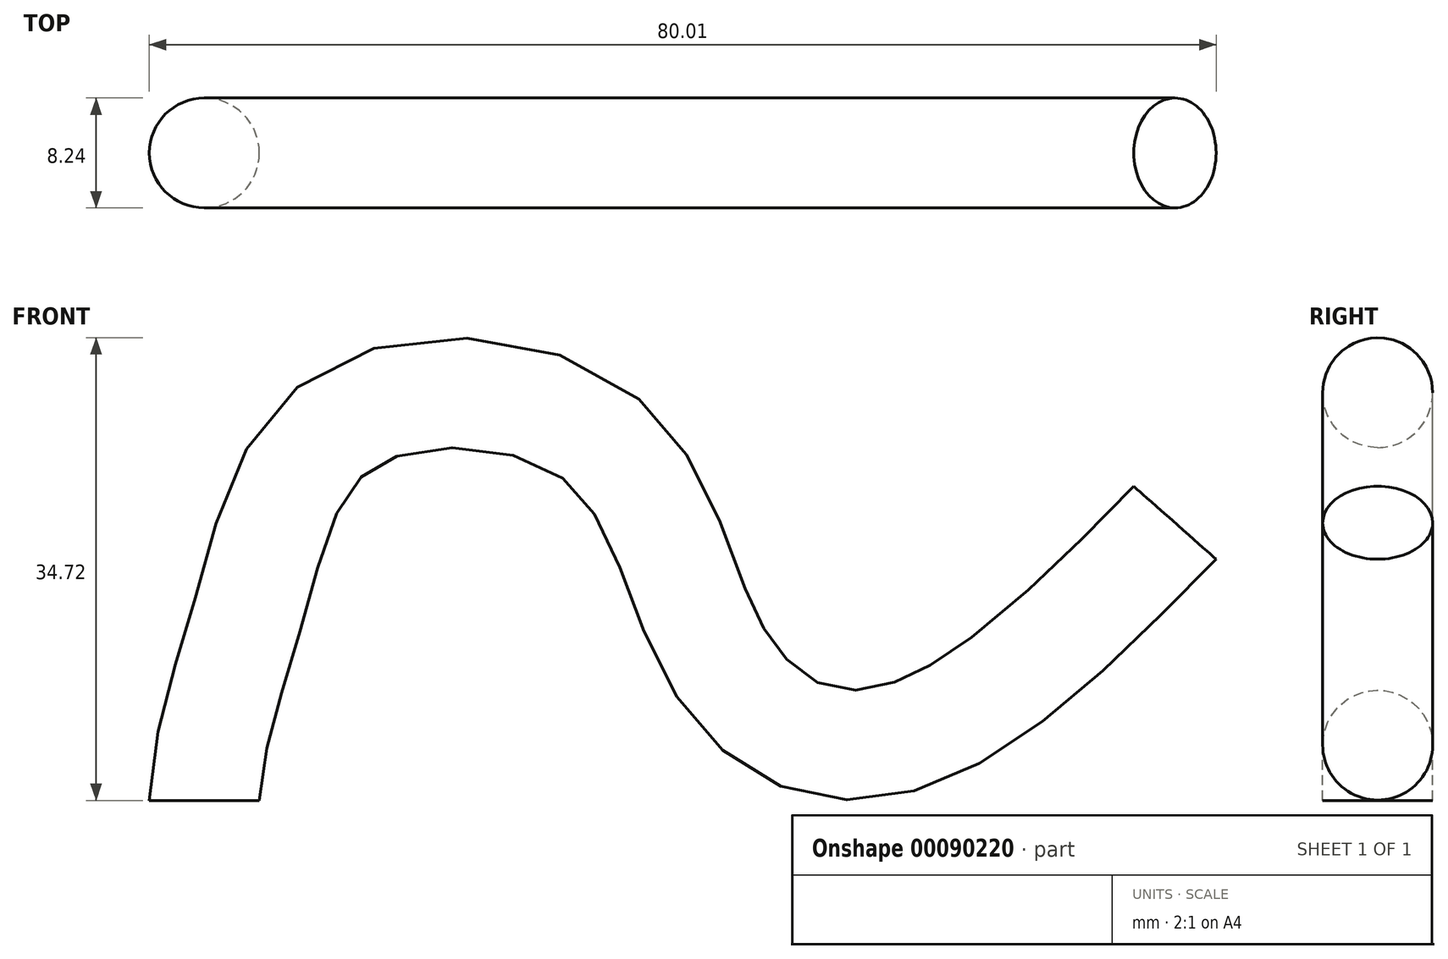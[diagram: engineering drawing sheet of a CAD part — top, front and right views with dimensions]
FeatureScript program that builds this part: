
annotation { "Feature Type Name" : "Feature", "Feature Type Description" : "" }
export const myFeature = defineFeature(function(context is Context, id is Id, definition is map)
    precondition{}
    {
        {
            var Q0;
            Q0=qCreatedBy(makeId("Front.planeOp"),FACE);
            var sketch = newSketch(context, id + "F0", { "sketchPlane" : qUnion([Q0])});
            skPoint(sketch, "E0", {"position": v(-50.34, 0) * mm});
            skPoint(sketch, "E1", {"position": v(-46.87, 14.66) * mm});
            skPoint(sketch, "E2", {"position": v(-39.95, 28.29) * mm});
            skPoint(sketch, "E3", {"position": v(-21.24, 27.13) * mm});
            skPoint(sketch, "E4", {"position": v(-12.93, 11.66) * mm});
            skPoint(sketch, "E5", {"position": v(-4.85, 4.27) * mm});
            skPoint(sketch, "E6", {"position": v(6, 6.35) * mm});
            skPoint(sketch, "E7", {"position": v(22.4, 20.67) * mm});
            skFitSpline(sketch, "E8", {"points": [v(-50.34, 0) * mm, v(-46.87, 14.66) * mm, v(-39.95, 28.29) * mm, v(-21.24, 27.13) * mm, v(-12.93, 11.66) * mm, v(-4.85, 4.27) * mm, v(6, 6.35) * mm, v(22.4, 20.67) * mm], "startDerivative": vector(5.26, 106.68) * mm, "endDerivative": vector(91.69, 93.82) * mm});
            skSolve(sketch);
        }
        {
            var Q0;
            Q0=qCreatedBy(makeId("Top.planeOp"),FACE);
            var sketch = newSketch(context, id + "F1", { "sketchPlane" : qUnion([Q0])});
            skCircle(sketch, "E9", {"center": v(-50.6, 0) * mm, "radius": 4.12 * mm});
            skSolve(sketch);
        }
        {
            var Q0;
            Q0=makeQuery(id+"F1.imprint","IMPRINT",FACE,{"disambiguationData":[TD([[makeQuery(id+"F1.imprint","IMPRINT",EDGE,{"derivedFrom":sQuery(id+"F1.wireOp",EDGE,"E9")}),1.0]])]});
            var Q1;
            Q1=sQuery(id+"F0.wireOp",EDGE,"E8");
            sweep(context, id + "F2", {"profiles" : qUnion([Q0]), "path" : qUnion([Q1])});
        }
    });
